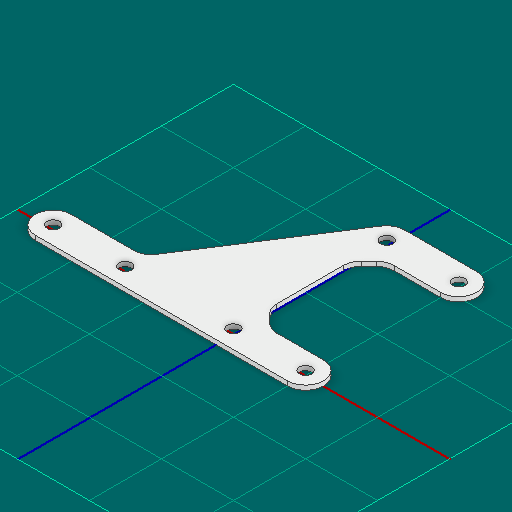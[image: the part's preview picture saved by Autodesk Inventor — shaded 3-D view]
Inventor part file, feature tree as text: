
AUTODESK INVENTOR PART (.ipt)
format: ipt  version: 2025 (Build 290162000, 162)  size: 126,976 bytes
history: native  units: in
note: dims shown in document units (in); Inventor stores cm internally (conversion verified against a paired STEP export)
features: other x3, extrude x1, sketch x1
ambient origin geometry x8: Origin, YZ Plane, XZ Plane, XY Plane, X Axis, Y Axis, Z Axis, Center Point
bodies: Solid1 (feature_tree)
feature tree (5):
  other  "Blocks"
  extrude  "Extrusion1"  Depth=0.0625in TaperAngle=0.0deg
  sketch  "Sketch1"  dims[d0=0.25in d1=0.25in d2=0.0625in d3=0.0in]
  other  "main"
  other  "main:1"
